AUTODESK INVENTOR PART (.ipt)
format: ipt  version: 2018 (Build 220112000, 112)  size: 235,520 bytes
history: native  units: in
note: dims shown in document units (in); Inventor stores cm internally (conversion verified against a paired STEP export)
features: extrude x1, sketch x1, other x1
ambient origin geometry x8: Origin, YZ Plane, XZ Plane, XY Plane, X Axis, Y Axis, Z Axis, Center Point
bodies: Solid1 (feature_tree)
feature tree (3):
  extrude  "Extrusion1"  Depth=25.15in
  sketch  "Sketch1"  dims[d0=2.0in d1=25.15in d2=0.3937in d3=0.0in d18=18.03in d21=7.5468in d31=12.575in d34=1.7022in d35=0.1165in]
  other  "Image2"
